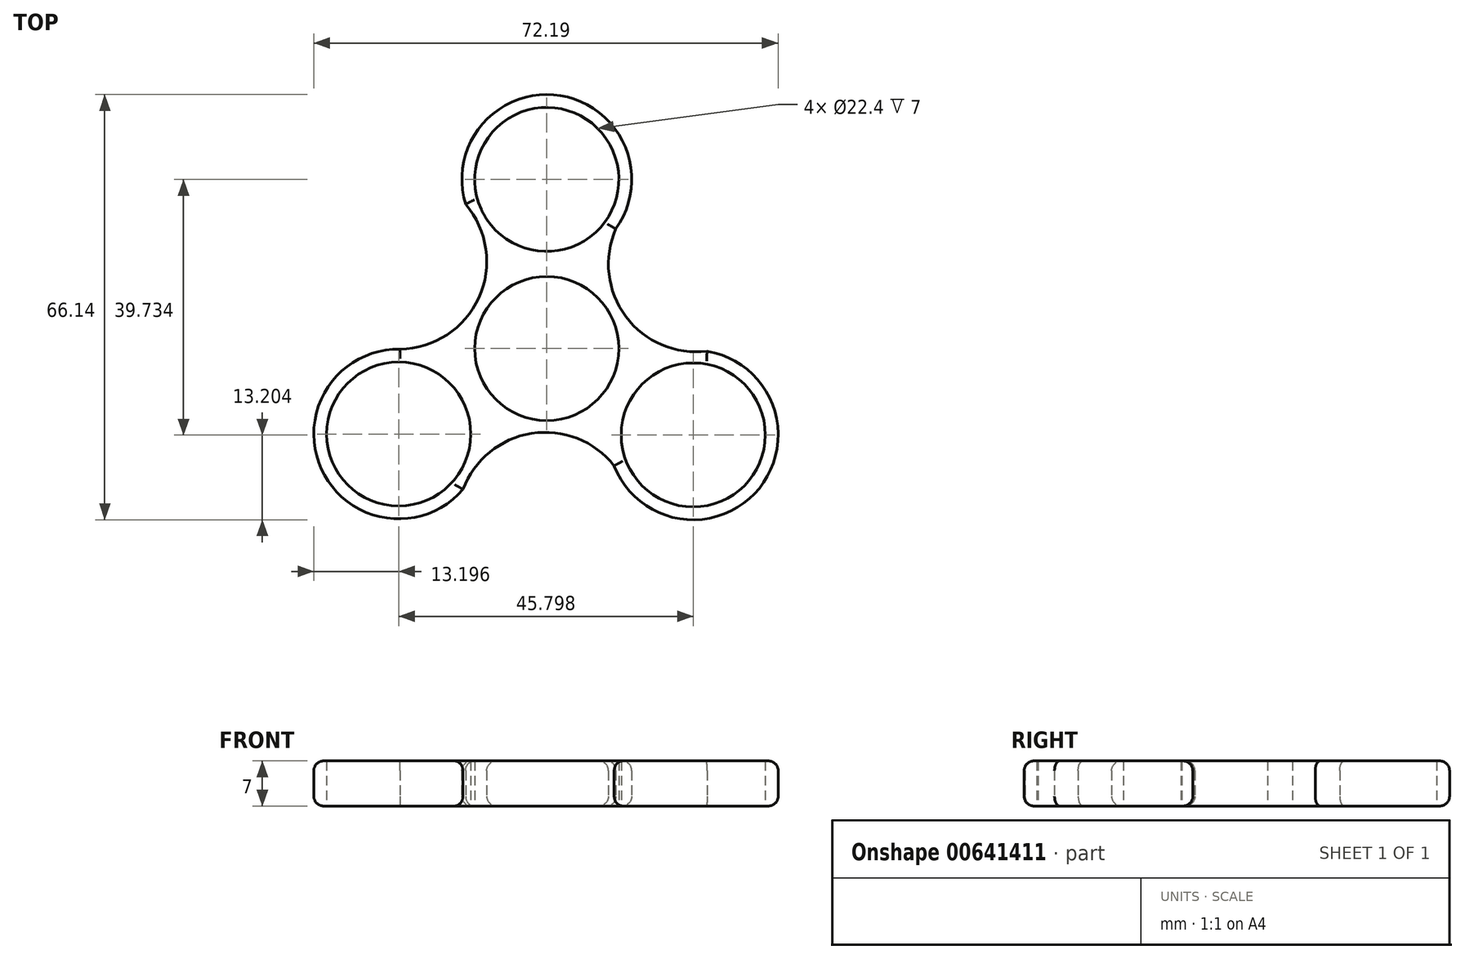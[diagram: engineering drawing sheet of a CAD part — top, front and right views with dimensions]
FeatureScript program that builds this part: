
annotation { "Feature Type Name" : "Feature", "Feature Type Description" : "" }
export const myFeature = defineFeature(function(context is Context, id is Id, definition is map)
    precondition{}
    {
        {
            var Q0;
            Q0=qCreatedBy(makeId("Top.planeOp"),FACE);
            var sketch = newSketch(context, id + "F0", { "sketchPlane" : qUnion([Q0])});
            skCircle(sketch, "E0", {"center": v(0, 0) * mm, "radius": 11.2 * mm});
            skArc(sketch, "E1", {"start": v(-10.55, 7.94) * mm, "mid": v(-11.37, 6.7) * mm, "end": v(-12.05, 5.39) * mm});
            skCircle(sketch, "E2", {"center": v(0, 26.3) * mm, "radius": 11.2 * mm});
            skArc(sketch, "E3", {"start": v(10.73, 18.6) * mm, "mid": v(-0.61, 39.48) * mm, "end": v(-9.97, 17.65) * mm});
            skArc(sketch, "E4.1.0", {"start": v(-22.8, -0.1) * mm, "mid": v(-33.9, -20.77) * mm, "end": v(-10.63, -17.83) * mm});
            skCircle(sketch, "E4.1.1", {"center": v(-23.02, -13.3) * mm, "radius": 11.2 * mm});
            skArc(sketch, "E4.2.0", {"start": v(10.48, -18.24) * mm, "mid": v(34.13, -20.16) * mm, "end": v(21.08, -0.35) * mm});
            skCircle(sketch, "E4.2.1", {"center": v(22.77, -13.44) * mm, "radius": 11.2 * mm});
            skPoint(sketch, "E4.center", {"position": v(-0.08, -0.14) * mm});
            skArc(sketch, "E5", {"start": v(-22.8, -0.1) * mm, "mid": v(-10.55, 7.92) * mm, "end": v(-12.62, 22.42) * mm});
            skArc(sketch, "E6.1.0", {"start": v(11.49, -19.7) * mm, "mid": v(-1.59, -13.1) * mm, "end": v(-13.11, -22.14) * mm});
            skArc(sketch, "E6.2.0", {"start": v(11.32, 19.8) * mm, "mid": v(12.14, 5.18) * mm, "end": v(25.73, -0.28) * mm});
            skArc(sketch, "E7.trimOffspring", {"start": v(12.15, 5.17) * mm, "mid": v(11.5, 6.5) * mm, "end": v(10.7, 7.74) * mm});
            skArc(sketch, "E8.trimOffspring", {"start": v(-1.6, -13.1) * mm, "mid": v(-0.12, -13.2) * mm, "end": v(1.36, -13.13) * mm});
            skSolve(sketch);
        }
        {
            var Q0;
            Q0=makeQuery(id+"F0.imprint","IMPRINT",FACE,{"disambiguationData":[TD([[makeQuery(id+"F0.imprint","IMPRINT",EDGE,{"derivedFrom":sQuery(id+"F0.wireOp",EDGE,"E0")}),-1.0]])]});
            extrude(context, id + "F1", {"entities" : qUnion([Q0]), "depth" : 7 * mm, "offsetDistance" : 25 * mm});
        }
        {
            var Q0;
            Q0=makeQuery(id+"F1.opExtrude","CAP_EDGE",EDGE,{"disambiguationData":[OSD([sQuery(id+"F0.wireOp",EDGE,"E3")])],"isStart":false});
            var Q1;
            Q1=makeQuery(id+"F1.opExtrude","CAP_EDGE",EDGE,{"disambiguationData":[OSD([sQuery(id+"F0.wireOp",EDGE,"E5")])],"isStart":false});
            var Q2;
            Q2=makeQuery(id+"F1.opExtrude","CAP_EDGE",EDGE,{"disambiguationData":[OSD([sQuery(id+"F0.wireOp",EDGE,"E4.1.0")])],"isStart":false});
            var Q3;
            Q3=makeQuery(id+"F1.opExtrude","CAP_EDGE",EDGE,{"disambiguationData":[OSD([sQuery(id+"F0.wireOp",EDGE,"E6.2.0")])],"isStart":false});
            var Q4;
            Q4=makeQuery(id+"F1.opExtrude","CAP_EDGE",EDGE,{"disambiguationData":[OSD([sQuery(id+"F0.wireOp",EDGE,"E4.2.0")])],"isStart":false});
            var Q5;
            Q5=makeQuery(id+"F1.opExtrude","CAP_EDGE",EDGE,{"disambiguationData":[OSD([sQuery(id+"F0.wireOp",EDGE,"E6.1.0")])],"isStart":false});
            fillet(context, id + "F2", {"entities" : qUnion([Q0, Q1, Q2, Q3, Q4, Q5]), "radius" : 1.5 * mm, "tangentPropagation" : true, "allowEdgeOverflow" : false});
        }
        {
            var Q0;
            Q0=makeQuery(id+"F1.opExtrude","CAP_EDGE",EDGE,{"disambiguationData":[OSD([sQuery(id+"F0.wireOp",EDGE,"E3")])],"isStart":true});
            var Q1;
            Q1=makeQuery(id+"F1.opExtrude","CAP_EDGE",EDGE,{"disambiguationData":[OSD([sQuery(id+"F0.wireOp",EDGE,"E5")])],"isStart":true});
            var Q2;
            Q2=makeQuery(id+"F1.opExtrude","CAP_EDGE",EDGE,{"disambiguationData":[OSD([sQuery(id+"F0.wireOp",EDGE,"E4.1.0")])],"isStart":true});
            var Q3;
            Q3=makeQuery(id+"F1.opExtrude","CAP_EDGE",EDGE,{"disambiguationData":[OSD([sQuery(id+"F0.wireOp",EDGE,"E6.1.0")])],"isStart":true});
            var Q4;
            Q4=makeQuery(id+"F1.opExtrude","CAP_EDGE",EDGE,{"disambiguationData":[OSD([sQuery(id+"F0.wireOp",EDGE,"E4.2.0")])],"isStart":true});
            var Q5;
            Q5=makeQuery(id+"F1.opExtrude","CAP_EDGE",EDGE,{"disambiguationData":[OSD([sQuery(id+"F0.wireOp",EDGE,"E6.2.0")])],"isStart":true});
            fillet(context, id + "F3", {"entities" : qUnion([Q0, Q1, Q2, Q3, Q4, Q5]), "radius" : 1.5 * mm, "tangentPropagation" : true, "allowEdgeOverflow" : false});
        }
    });
